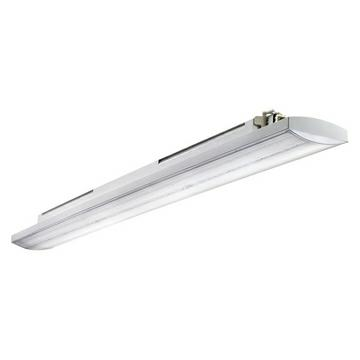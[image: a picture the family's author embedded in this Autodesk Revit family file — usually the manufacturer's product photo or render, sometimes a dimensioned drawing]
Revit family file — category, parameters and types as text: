
# Revit family: Lighting-Industrial-GEWISS-SMART[3]PLUS-WATERTIGHT-LED-EMERGENCY_TRANSPARENT_1600mm
name_source: partatom
category: Apparecchi per illuminazione
units: mm (PartAtom-declared; Revit-internal decimal feet)

## family parameters
Condiviso = No
Host = Superficie
Punto di calcolo locali = No
Quota connettore circolare = Usa diametro
Sorgente d'illuminazione = No
Taglio con vuoti quando caricato = No
Tipo di parte = Normale

## types (1)
- Lighting-Industrial-GEWISS-SMART[3]PLUS-WATERTIGHT-LED-EMERGENCY_TRANSPARENT_1600mm
    Application = Indoor
    Carico apparente = 53 VA
    Catalogue = LIGHTING
    Catalogue Range = SMART[3] PLUS
    Colour temperature = 5700 K (CRI > 90)
    Colour temperature: = 5700 K (CRI > 90)
    Commenti sul wattaggio = 53W
    Descrizione = SMART3 PLUS 1600 EMERG DT1+DT6 HE TRASP 9 57
    Efficiency class of integrated LEDs = A ÷ A++
    Electrocod = 2434
    Ganci = Alluminio
    Glow Wire Test = 850°C
    IDF = 45533622-a399-43a6-a2ce-b7e15d4ad49e
    IDT = e64a989e-ee90-4262-bf48-8a52b238cc43
    IP degree = IP66/IP69
    Immagine tipo = GWS3258T30K.jpg
    Insulation class = II
    Lamp- = LED
    Lampada = LED
    Length- = 1600 mm
    Lumen output (lm) = 5900
    Lunghezza Lampada = 1600 mm
    Modello = GWS3325AT957
    Numero poli = 2
    Operating temperature: = ND
    Produttore = GEWISS S.p.A.
    Prospetto di default = 1219 mm
    SEO = Ceiling
    Schermo. = Led Acceso
    Shield type = Transparent
    Shock resistance = IK08
    Stampa 1_100 = Sì
    Stampa 1_200 = No
    Struttura = GRIGIO
    System power = 50 W
    Technical sheet = https://www.gewiss.com
    Type of light source = LED - Not replaceable
    URL = https://www.gewiss.com
    Version file RFA = 20.0
    Voltage- = 220-240 V
    Warranty = ND
    Working temperature = ND
